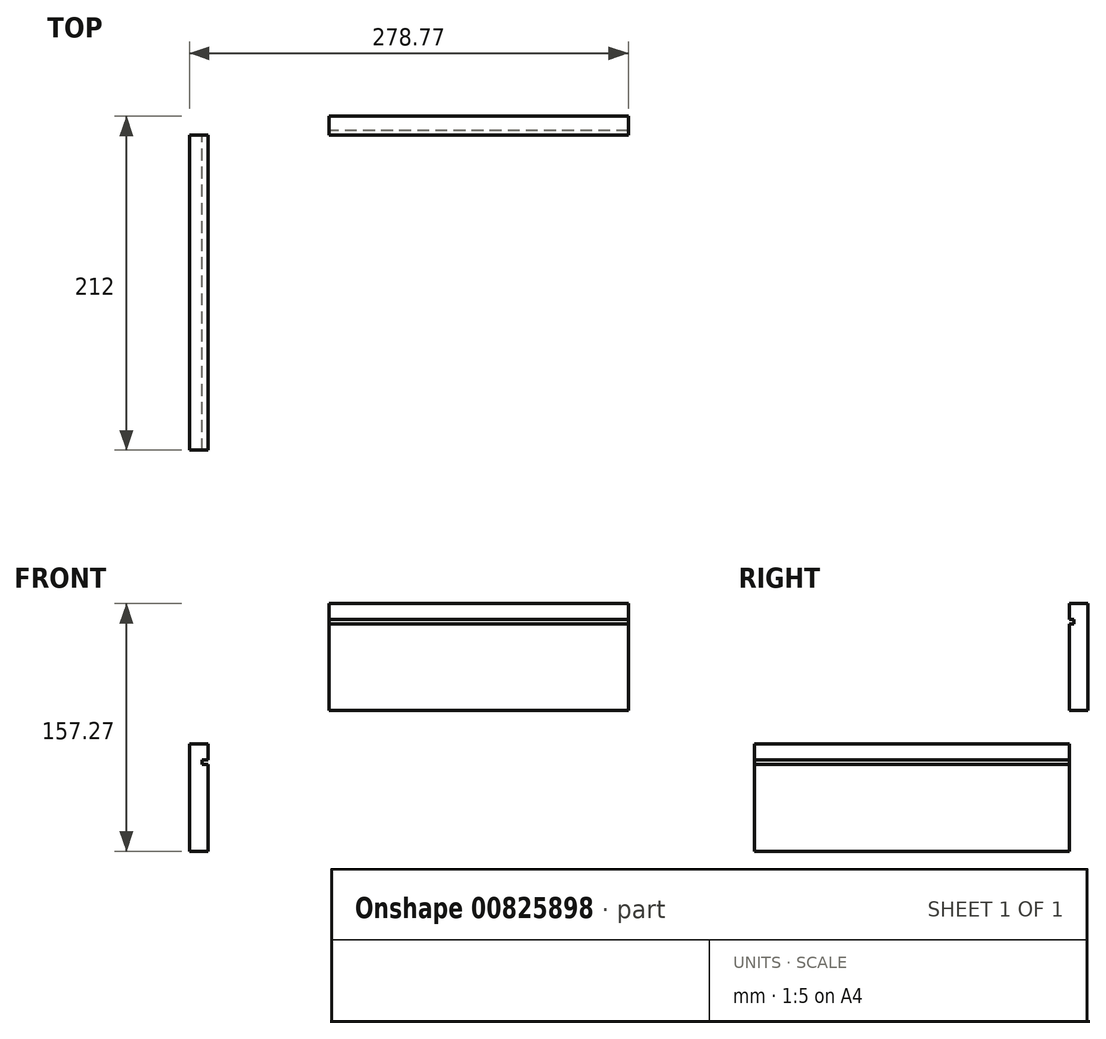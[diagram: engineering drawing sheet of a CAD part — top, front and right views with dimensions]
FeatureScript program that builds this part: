
annotation { "Feature Type Name" : "Feature", "Feature Type Description" : "" }
export const myFeature = defineFeature(function(context is Context, id is Id, definition is map)
    precondition{}
    {
        {
            var Q0;
            Q0=qCreatedBy(makeId("Right.planeOp"),FACE);
            var sketch = newSketch(context, id + "F0", { "sketchPlane" : qUnion([Q0])});
            skLineSegment(sketch, "E0.bottom", {"start": v(0, 46.77) * mm, "end": v(12, 46.77) * mm});
            skLineSegment(sketch, "E0.top", {"start": v(0, -21.23) * mm, "end": v(12, -21.23) * mm});
            skLineSegment(sketch, "E0.left", {"start": v(0, 46.77) * mm, "end": v(0, 36.77) * mm});
            skLineSegment(sketch, "E0.right", {"start": v(12, 46.77) * mm, "end": v(12, -21.23) * mm});
            skLineSegment(sketch, "E1", {"start": v(0, 36.77) * mm, "end": v(3, 36.77) * mm});
            skLineSegment(sketch, "E2", {"start": v(3, 36.77) * mm, "end": v(3, 33.77) * mm});
            skLineSegment(sketch, "E3", {"start": v(3, 33.77) * mm, "end": v(0, 33.77) * mm});
            skLineSegment(sketch, "E4.trimOffspring", {"start": v(0, 33.77) * mm, "end": v(0, -21.23) * mm});
            skLineSegment(sketch, "E5", {"start": v(0, 36.77) * mm, "end": v(0, 46.77) * mm});
            skSolve(sketch);
        }
        {
            var Q0;
            Q0 = qSketchRegion(id + "F0", true);
            extrude(context, id + "F1", {"entities" : qUnion([Q0]), "depth" : 190 * mm, "offsetDistance" : 25 * mm});
        }
        {
            var Q0;
            Q0=qCreatedBy(makeId("Front.planeOp"),FACE);
            var sketch = newSketch(context, id + "F2", { "sketchPlane" : qUnion([Q0])});
            skLineSegment(sketch, "E6.bottom", {"start": v(-88.77, -42.5) * mm, "end": v(-76.77, -42.5) * mm});
            skLineSegment(sketch, "E6.top", {"start": v(-88.77, -110.5) * mm, "end": v(-76.77, -110.5) * mm});
            skLineSegment(sketch, "E6.left", {"start": v(-88.77, -42.5) * mm, "end": v(-88.77, -110.5) * mm});
            skLineSegment(sketch, "E6.right", {"start": v(-76.77, -42.5) * mm, "end": v(-76.77, -52.5) * mm});
            skLineSegment(sketch, "E7.bottom", {"start": v(-76.77, -52.5) * mm, "end": v(-80.6, -52.5) * mm});
            skLineSegment(sketch, "E7.top", {"start": v(-76.77, -55.5) * mm, "end": v(-80.6, -55.5) * mm});
            skLineSegment(sketch, "E7.right", {"start": v(-80.6, -52.5) * mm, "end": v(-80.6, -55.5) * mm});
            skLineSegment(sketch, "E8.trimOffspring", {"start": v(-76.77, -55.5) * mm, "end": v(-76.77, -110.5) * mm});
            skSolve(sketch);
        }
        {
            var Q0;
            Q0 = qSketchRegion(id + "F2", true);
            extrude(context, id + "F3", {"entities" : qUnion([Q0]), "depth" : 200 * mm, "offsetDistance" : 25 * mm});
        }
    });
